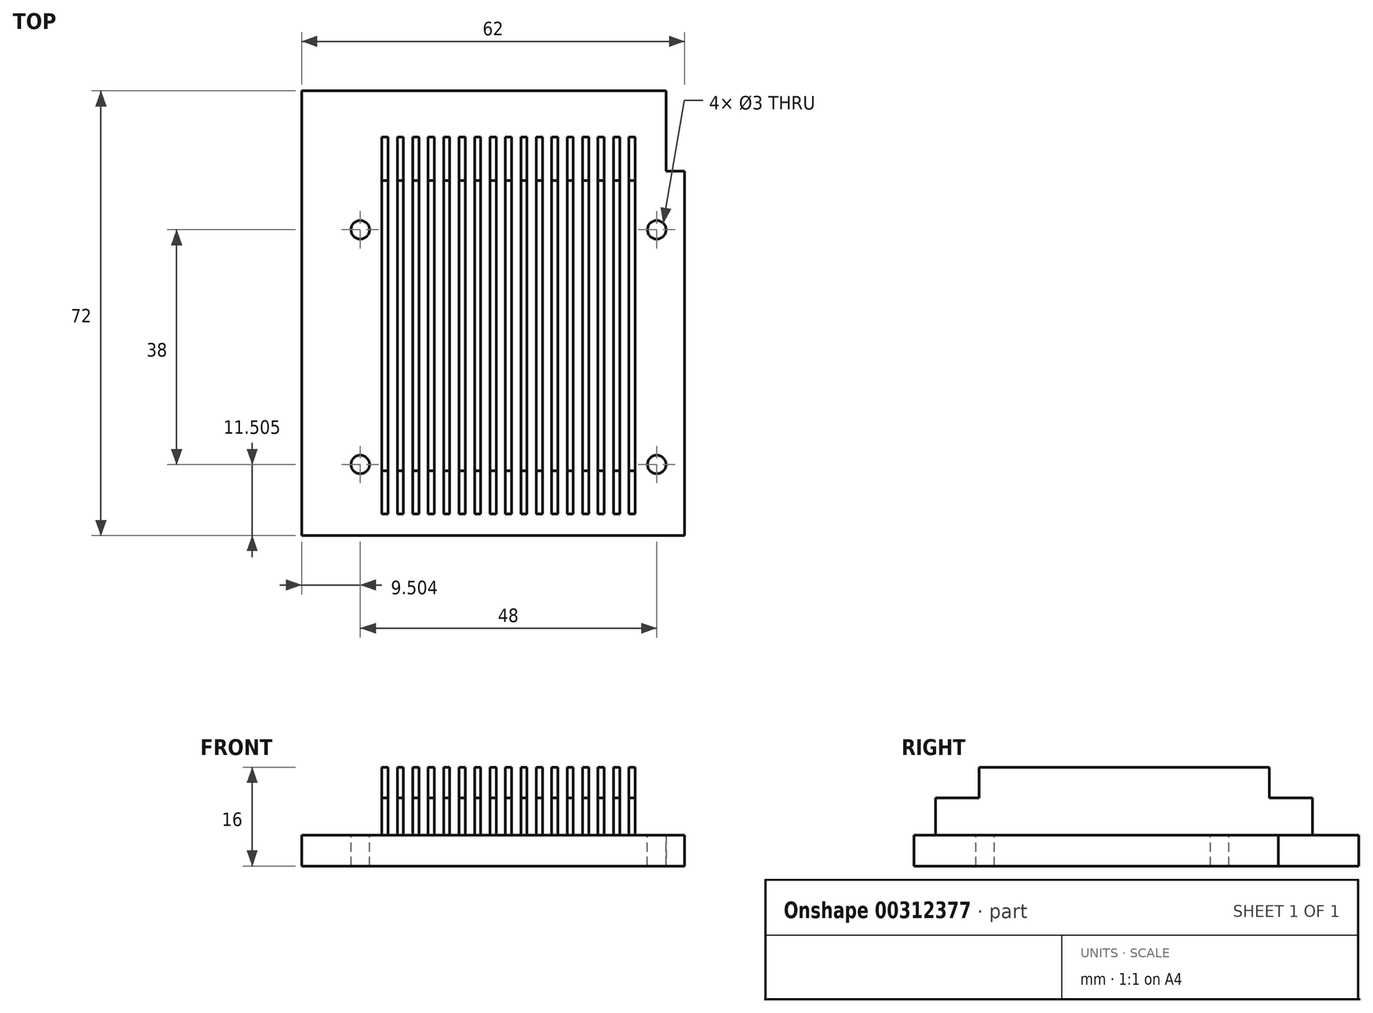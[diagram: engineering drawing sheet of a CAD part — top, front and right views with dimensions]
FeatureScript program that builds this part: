
annotation { "Feature Type Name" : "Feature", "Feature Type Description" : "" }
export const myFeature = defineFeature(function(context is Context, id is Id, definition is map)
    precondition{}
    {
        {
            var Q0;
            Q0=qCreatedBy(makeId("Top.planeOp"),FACE);
            var sketch = newSketch(context, id + "F0", { "sketchPlane" : qUnion([Q0])});
            skLineSegment(sketch, "E0", {"start": v(-50.22, 49.8) * mm, "end": v(-50.22, -22.2) * mm});
            skLineSegment(sketch, "E1", {"start": v(-50.22, 49.8) * mm, "end": v(8.78, 49.8) * mm});
            skLineSegment(sketch, "E2", {"start": v(8.78, 49.8) * mm, "end": v(8.78, 36.8) * mm});
            skLineSegment(sketch, "E3", {"start": v(8.78, 36.8) * mm, "end": v(11.78, 36.8) * mm});
            skLineSegment(sketch, "E4", {"start": v(11.78, 36.8) * mm, "end": v(11.78, -22.2) * mm});
            skLineSegment(sketch, "E5", {"start": v(-50.22, -22.2) * mm, "end": v(11.78, -22.2) * mm});
            skSolve(sketch);
        }
        {
            var Q0;
            Q0=makeQuery(id+"F0.imprint","IMPRINT",FACE,{"disambiguationData":[TD([[makeQuery(id+"F0.imprint","IMPRINT",EDGE,{"derivedFrom":sQuery(id+"F0.wireOp",EDGE,"E0")}),1.0]])]});
            extrude(context, id + "F1", {"entities" : qUnion([Q0]), "depth" : 5 * mm});
        }
        {
            var Q0;
            Q0=makeQuery(id+"F1.opExtrude","CAP_FACE",FACE,{"disambiguationData":[OSD([sQuery(id+"F0.wireOp",EDGE,"E0"),sQuery(id+"F0.wireOp",EDGE,"E1"),sQuery(id+"F0.wireOp",EDGE,"E2"),sQuery(id+"F0.wireOp",EDGE,"E3"),sQuery(id+"F0.wireOp",EDGE,"E4"),sQuery(id+"F0.wireOp",EDGE,"E5")])],"isStart":false});
            var sketch = newSketch(context, id + "F2", { "sketchPlane" : qUnion([Q0])});
            skLineSegment(sketch, "E6", {"start": v(-50.22, 13.8) * mm, "end": v(-37.22, 13.8) * mm});
            skPoint(sketch, "E6.endSnap0", {"position": v(-50.22, 13.8) * mm});
            skLineSegment(sketch, "E7", {"start": v(-20.72, 49.8) * mm, "end": v(-20.72, 42.3) * mm});
            skLineSegment(sketch, "E8", {"start": v(-19.22, -22.2) * mm, "end": v(-19.22, -18.7) * mm});
            skLineSegment(sketch, "E9", {"start": v(-37.22, 13.8) * mm, "end": v(-37.22, 42.3) * mm});
            skLineSegment(sketch, "E10", {"start": v(-37.22, 42.3) * mm, "end": v(-36.22, 42.3) * mm});
            skLineSegment(sketch, "E11", {"start": v(-36.22, 42.3) * mm, "end": v(-36.22, -18.7) * mm});
            skLineSegment(sketch, "E12", {"start": v(-36.22, -18.7) * mm, "end": v(-37.22, -18.7) * mm});
            skLineSegment(sketch, "E13", {"start": v(-37.22, -18.7) * mm, "end": v(-37.22, 13.8) * mm});
            skLineSegment(sketch, "E14", {"start": v(-36.22, 35.3) * mm, "end": v(-37.22, 35.3) * mm});
            skLineSegment(sketch, "E15", {"start": v(-36.22, -11.7) * mm, "end": v(-37.22, -11.7) * mm});
            skLineSegment(sketch, "E16.1.0.0", {"start": v(-33.72, 42.3) * mm, "end": v(-33.72, -18.7) * mm});
            skLineSegment(sketch, "E16.1.0.1", {"start": v(-34.72, 13.8) * mm, "end": v(-34.72, 42.3) * mm});
            skLineSegment(sketch, "E16.1.0.2", {"start": v(-34.72, -18.7) * mm, "end": v(-34.72, 13.8) * mm});
            skLineSegment(sketch, "E16.1.0.3", {"start": v(-33.72, 35.3) * mm, "end": v(-34.72, 35.3) * mm});
            skLineSegment(sketch, "E16.1.0.4", {"start": v(-33.72, -11.7) * mm, "end": v(-34.72, -11.7) * mm});
            skLineSegment(sketch, "E16.1.0.5", {"start": v(-33.72, -18.7) * mm, "end": v(-34.72, -18.7) * mm});
            skLineSegment(sketch, "E16.1.0.6", {"start": v(-34.72, 42.3) * mm, "end": v(-33.72, 42.3) * mm});
            skLineSegment(sketch, "E16.2.0.0", {"start": v(-31.22, 42.3) * mm, "end": v(-31.22, -18.7) * mm});
            skLineSegment(sketch, "E16.2.0.1", {"start": v(-32.22, 13.8) * mm, "end": v(-32.22, 42.3) * mm});
            skLineSegment(sketch, "E16.2.0.2", {"start": v(-32.22, -18.7) * mm, "end": v(-32.22, 13.8) * mm});
            skLineSegment(sketch, "E16.2.0.3", {"start": v(-31.22, 35.3) * mm, "end": v(-32.22, 35.3) * mm});
            skLineSegment(sketch, "E16.2.0.4", {"start": v(-31.22, -11.7) * mm, "end": v(-32.22, -11.7) * mm});
            skLineSegment(sketch, "E16.2.0.5", {"start": v(-31.22, -18.7) * mm, "end": v(-32.22, -18.7) * mm});
            skLineSegment(sketch, "E16.2.0.6", {"start": v(-32.22, 42.3) * mm, "end": v(-31.22, 42.3) * mm});
            skLineSegment(sketch, "E16.3.0.0", {"start": v(-28.72, 42.3) * mm, "end": v(-28.72, -18.7) * mm});
            skLineSegment(sketch, "E16.3.0.1", {"start": v(-29.72, 13.8) * mm, "end": v(-29.72, 42.3) * mm});
            skLineSegment(sketch, "E16.3.0.2", {"start": v(-29.72, -18.7) * mm, "end": v(-29.72, 13.8) * mm});
            skLineSegment(sketch, "E16.3.0.3", {"start": v(-28.72, 35.3) * mm, "end": v(-29.72, 35.3) * mm});
            skLineSegment(sketch, "E16.3.0.4", {"start": v(-28.72, -11.7) * mm, "end": v(-29.72, -11.7) * mm});
            skLineSegment(sketch, "E16.3.0.5", {"start": v(-28.72, -18.7) * mm, "end": v(-29.72, -18.7) * mm});
            skLineSegment(sketch, "E16.3.0.6", {"start": v(-29.72, 42.3) * mm, "end": v(-28.72, 42.3) * mm});
            skLineSegment(sketch, "E16.4.0.0", {"start": v(-26.22, 42.3) * mm, "end": v(-26.22, -18.7) * mm});
            skLineSegment(sketch, "E16.4.0.1", {"start": v(-27.22, 13.8) * mm, "end": v(-27.22, 42.3) * mm});
            skLineSegment(sketch, "E16.4.0.2", {"start": v(-27.22, -18.7) * mm, "end": v(-27.22, 13.8) * mm});
            skLineSegment(sketch, "E16.4.0.3", {"start": v(-26.22, 35.3) * mm, "end": v(-27.22, 35.3) * mm});
            skLineSegment(sketch, "E16.4.0.4", {"start": v(-26.22, -11.7) * mm, "end": v(-27.22, -11.7) * mm});
            skLineSegment(sketch, "E16.4.0.5", {"start": v(-26.22, -18.7) * mm, "end": v(-27.22, -18.7) * mm});
            skLineSegment(sketch, "E16.4.0.6", {"start": v(-27.22, 42.3) * mm, "end": v(-26.22, 42.3) * mm});
            skLineSegment(sketch, "E16.5.0.0", {"start": v(-23.72, 42.3) * mm, "end": v(-23.72, -18.7) * mm});
            skLineSegment(sketch, "E16.5.0.1", {"start": v(-24.72, 13.8) * mm, "end": v(-24.72, 42.3) * mm});
            skLineSegment(sketch, "E16.5.0.2", {"start": v(-24.72, -18.7) * mm, "end": v(-24.72, 13.8) * mm});
            skLineSegment(sketch, "E16.5.0.3", {"start": v(-23.72, 35.3) * mm, "end": v(-24.72, 35.3) * mm});
            skLineSegment(sketch, "E16.5.0.4", {"start": v(-23.72, -11.7) * mm, "end": v(-24.72, -11.7) * mm});
            skLineSegment(sketch, "E16.5.0.5", {"start": v(-23.72, -18.7) * mm, "end": v(-24.72, -18.7) * mm});
            skLineSegment(sketch, "E16.5.0.6", {"start": v(-24.72, 42.3) * mm, "end": v(-23.72, 42.3) * mm});
            skLineSegment(sketch, "E16.6.0.0", {"start": v(-21.22, 42.3) * mm, "end": v(-21.22, -18.7) * mm});
            skLineSegment(sketch, "E16.6.0.1", {"start": v(-22.22, 13.8) * mm, "end": v(-22.22, 42.3) * mm});
            skLineSegment(sketch, "E16.6.0.2", {"start": v(-22.22, -18.7) * mm, "end": v(-22.22, 13.8) * mm});
            skLineSegment(sketch, "E16.6.0.3", {"start": v(-21.22, 35.3) * mm, "end": v(-22.22, 35.3) * mm});
            skLineSegment(sketch, "E16.6.0.4", {"start": v(-21.22, -11.7) * mm, "end": v(-22.22, -11.7) * mm});
            skLineSegment(sketch, "E16.6.0.5", {"start": v(-21.22, -18.7) * mm, "end": v(-22.22, -18.7) * mm});
            skLineSegment(sketch, "E16.6.0.6", {"start": v(-22.22, 42.3) * mm, "end": v(-21.22, 42.3) * mm});
            skLineSegment(sketch, "E16.7.0.0", {"start": v(-18.72, 42.3) * mm, "end": v(-18.72, -18.7) * mm});
            skLineSegment(sketch, "E16.7.0.1", {"start": v(-19.72, 13.8) * mm, "end": v(-19.72, 42.3) * mm});
            skLineSegment(sketch, "E16.7.0.2", {"start": v(-19.72, -18.7) * mm, "end": v(-19.72, 13.8) * mm});
            skLineSegment(sketch, "E16.7.0.3", {"start": v(-18.72, 35.3) * mm, "end": v(-19.72, 35.3) * mm});
            skLineSegment(sketch, "E16.7.0.4", {"start": v(-18.72, -11.7) * mm, "end": v(-19.72, -11.7) * mm});
            skLineSegment(sketch, "E16.7.0.5", {"start": v(-18.72, -18.7) * mm, "end": v(-19.72, -18.7) * mm});
            skLineSegment(sketch, "E16.7.0.6", {"start": v(-19.72, 42.3) * mm, "end": v(-18.72, 42.3) * mm});
            skLineSegment(sketch, "E16.8.0.0", {"start": v(-16.22, 42.3) * mm, "end": v(-16.22, -18.7) * mm});
            skLineSegment(sketch, "E16.8.0.1", {"start": v(-17.22, 13.8) * mm, "end": v(-17.22, 42.3) * mm});
            skLineSegment(sketch, "E16.8.0.2", {"start": v(-17.22, -18.7) * mm, "end": v(-17.22, 13.8) * mm});
            skLineSegment(sketch, "E16.8.0.3", {"start": v(-16.22, 35.3) * mm, "end": v(-17.22, 35.3) * mm});
            skLineSegment(sketch, "E16.8.0.4", {"start": v(-16.22, -11.7) * mm, "end": v(-17.22, -11.7) * mm});
            skLineSegment(sketch, "E16.8.0.5", {"start": v(-16.22, -18.7) * mm, "end": v(-17.22, -18.7) * mm});
            skLineSegment(sketch, "E16.8.0.6", {"start": v(-17.22, 42.3) * mm, "end": v(-16.22, 42.3) * mm});
            skLineSegment(sketch, "E16.9.0.0", {"start": v(-13.72, 42.3) * mm, "end": v(-13.72, -18.7) * mm});
            skLineSegment(sketch, "E16.9.0.1", {"start": v(-14.72, 13.8) * mm, "end": v(-14.72, 42.3) * mm});
            skLineSegment(sketch, "E16.9.0.2", {"start": v(-14.72, -18.7) * mm, "end": v(-14.72, 13.8) * mm});
            skLineSegment(sketch, "E16.9.0.3", {"start": v(-13.72, 35.3) * mm, "end": v(-14.72, 35.3) * mm});
            skLineSegment(sketch, "E16.9.0.4", {"start": v(-13.72, -11.7) * mm, "end": v(-14.72, -11.7) * mm});
            skLineSegment(sketch, "E16.9.0.5", {"start": v(-13.72, -18.7) * mm, "end": v(-14.72, -18.7) * mm});
            skLineSegment(sketch, "E16.9.0.6", {"start": v(-14.72, 42.3) * mm, "end": v(-13.72, 42.3) * mm});
            skLineSegment(sketch, "E16.10.0.0", {"start": v(-11.22, 42.3) * mm, "end": v(-11.22, -18.7) * mm});
            skLineSegment(sketch, "E16.10.0.1", {"start": v(-12.22, 13.8) * mm, "end": v(-12.22, 42.3) * mm});
            skLineSegment(sketch, "E16.10.0.2", {"start": v(-12.22, -18.7) * mm, "end": v(-12.22, 13.8) * mm});
            skLineSegment(sketch, "E16.10.0.3", {"start": v(-11.22, 35.3) * mm, "end": v(-12.22, 35.3) * mm});
            skLineSegment(sketch, "E16.10.0.4", {"start": v(-11.22, -11.7) * mm, "end": v(-12.22, -11.7) * mm});
            skLineSegment(sketch, "E16.10.0.5", {"start": v(-11.22, -18.7) * mm, "end": v(-12.22, -18.7) * mm});
            skLineSegment(sketch, "E16.10.0.6", {"start": v(-12.22, 42.3) * mm, "end": v(-11.22, 42.3) * mm});
            skLineSegment(sketch, "E16.11.0.0", {"start": v(-8.72, 42.3) * mm, "end": v(-8.72, -18.7) * mm});
            skLineSegment(sketch, "E16.11.0.1", {"start": v(-9.72, 13.8) * mm, "end": v(-9.72, 42.3) * mm});
            skLineSegment(sketch, "E16.11.0.2", {"start": v(-9.72, -18.7) * mm, "end": v(-9.72, 13.8) * mm});
            skLineSegment(sketch, "E16.11.0.3", {"start": v(-8.72, 35.3) * mm, "end": v(-9.72, 35.3) * mm});
            skLineSegment(sketch, "E16.11.0.4", {"start": v(-8.72, -11.7) * mm, "end": v(-9.72, -11.7) * mm});
            skLineSegment(sketch, "E16.11.0.5", {"start": v(-8.72, -18.7) * mm, "end": v(-9.72, -18.7) * mm});
            skLineSegment(sketch, "E16.11.0.6", {"start": v(-9.72, 42.3) * mm, "end": v(-8.72, 42.3) * mm});
            skLineSegment(sketch, "E16.12.0.0", {"start": v(-6.22, 42.3) * mm, "end": v(-6.22, -18.7) * mm});
            skLineSegment(sketch, "E16.12.0.1", {"start": v(-7.22, 13.8) * mm, "end": v(-7.22, 42.3) * mm});
            skLineSegment(sketch, "E16.12.0.2", {"start": v(-7.22, -18.7) * mm, "end": v(-7.22, 13.8) * mm});
            skLineSegment(sketch, "E16.12.0.3", {"start": v(-6.22, 35.3) * mm, "end": v(-7.22, 35.3) * mm});
            skLineSegment(sketch, "E16.12.0.4", {"start": v(-6.22, -11.7) * mm, "end": v(-7.22, -11.7) * mm});
            skLineSegment(sketch, "E16.12.0.5", {"start": v(-6.22, -18.7) * mm, "end": v(-7.22, -18.7) * mm});
            skLineSegment(sketch, "E16.12.0.6", {"start": v(-7.22, 42.3) * mm, "end": v(-6.22, 42.3) * mm});
            skLineSegment(sketch, "E16.13.0.0", {"start": v(-3.72, 42.3) * mm, "end": v(-3.72, -18.7) * mm});
            skLineSegment(sketch, "E16.13.0.1", {"start": v(-4.72, 13.8) * mm, "end": v(-4.72, 42.3) * mm});
            skLineSegment(sketch, "E16.13.0.2", {"start": v(-4.72, -18.7) * mm, "end": v(-4.72, 13.8) * mm});
            skLineSegment(sketch, "E16.13.0.3", {"start": v(-3.72, 35.3) * mm, "end": v(-4.72, 35.3) * mm});
            skLineSegment(sketch, "E16.13.0.4", {"start": v(-3.72, -11.7) * mm, "end": v(-4.72, -11.7) * mm});
            skLineSegment(sketch, "E16.13.0.5", {"start": v(-3.72, -18.7) * mm, "end": v(-4.72, -18.7) * mm});
            skLineSegment(sketch, "E16.13.0.6", {"start": v(-4.72, 42.3) * mm, "end": v(-3.72, 42.3) * mm});
            skLineSegment(sketch, "E16.14.0.0", {"start": v(-1.22, 42.3) * mm, "end": v(-1.22, -18.7) * mm});
            skLineSegment(sketch, "E16.14.0.1", {"start": v(-2.22, 13.8) * mm, "end": v(-2.22, 42.3) * mm});
            skLineSegment(sketch, "E16.14.0.2", {"start": v(-2.22, -18.7) * mm, "end": v(-2.22, 13.8) * mm});
            skLineSegment(sketch, "E16.14.0.3", {"start": v(-1.22, 35.3) * mm, "end": v(-2.22, 35.3) * mm});
            skLineSegment(sketch, "E16.14.0.4", {"start": v(-1.22, -11.7) * mm, "end": v(-2.22, -11.7) * mm});
            skLineSegment(sketch, "E16.14.0.5", {"start": v(-1.22, -18.7) * mm, "end": v(-2.22, -18.7) * mm});
            skLineSegment(sketch, "E16.14.0.6", {"start": v(-2.22, 42.3) * mm, "end": v(-1.22, 42.3) * mm});
            skLineSegment(sketch, "E16.15.0.0", {"start": v(1.28, 42.3) * mm, "end": v(1.28, -18.7) * mm});
            skLineSegment(sketch, "E16.15.0.1", {"start": v(0.28, 13.8) * mm, "end": v(0.28, 42.3) * mm});
            skLineSegment(sketch, "E16.15.0.2", {"start": v(0.28, -18.7) * mm, "end": v(0.28, 13.8) * mm});
            skLineSegment(sketch, "E16.15.0.3", {"start": v(1.28, 35.3) * mm, "end": v(0.28, 35.3) * mm});
            skLineSegment(sketch, "E16.15.0.4", {"start": v(1.28, -11.7) * mm, "end": v(0.28, -11.7) * mm});
            skLineSegment(sketch, "E16.15.0.5", {"start": v(1.28, -18.7) * mm, "end": v(0.28, -18.7) * mm});
            skLineSegment(sketch, "E16.15.0.6", {"start": v(0.28, 42.3) * mm, "end": v(1.28, 42.3) * mm});
            skLineSegment(sketch, "E16.16.0.0", {"start": v(3.78, 42.3) * mm, "end": v(3.78, -18.7) * mm});
            skLineSegment(sketch, "E16.16.0.1", {"start": v(2.78, 13.8) * mm, "end": v(2.78, 42.3) * mm});
            skLineSegment(sketch, "E16.16.0.2", {"start": v(2.78, -18.7) * mm, "end": v(2.78, 13.8) * mm});
            skLineSegment(sketch, "E16.16.0.3", {"start": v(3.78, 35.3) * mm, "end": v(2.78, 35.3) * mm});
            skLineSegment(sketch, "E16.16.0.4", {"start": v(3.78, -11.7) * mm, "end": v(2.78, -11.7) * mm});
            skLineSegment(sketch, "E16.16.0.5", {"start": v(3.78, -18.7) * mm, "end": v(2.78, -18.7) * mm});
            skLineSegment(sketch, "E16.16.0.6", {"start": v(2.78, 42.3) * mm, "end": v(3.78, 42.3) * mm});
            skLineSegment(sketch, "E16.direction1", {"start": v(-37.22, -18.7) * mm, "end": v(-34.72, -18.7) * mm, "construction": true});
            skLineSegment(sketch, "E17", {"start": v(-50.22, -22.2) * mm, "end": v(-40.72, -22.2) * mm});
            skLineSegment(sketch, "E18", {"start": v(-40.72, -22.2) * mm, "end": v(-40.72, -10.7) * mm});
            skLineSegment(sketch, "E19", {"start": v(-40.72, -10.7) * mm, "end": v(-40.72, 27.3) * mm});
            skLineSegment(sketch, "E20", {"start": v(11.78, -22.2) * mm, "end": v(7.28, -22.2) * mm});
            skLineSegment(sketch, "E21", {"start": v(7.28, -22.2) * mm, "end": v(7.28, -10.7) * mm});
            skLineSegment(sketch, "E22", {"start": v(7.28, -10.7) * mm, "end": v(7.28, 27.3) * mm});
            skSolve(sketch);
        }
        {
            var Q0;
            {var subQ4=sQuery(id+"F2.wireOp",EDGE,"E14");Q0=makeQuery(id+"F2.imprint","IMPRINT",FACE,{"disambiguationData":[TD([[makeQuery(id+"F2.imprint","IMPRINT",EDGE,{"derivedFrom":subQ4}),1.0]])]});}
            var Q1;
            {var subQ0=sQuery(id+"F2.wireOp",EDGE,"E16.1.0.3");Q1=makeQuery(id+"F2.imprint","IMPRINT",FACE,{"disambiguationData":[TD([[makeQuery(id+"F2.imprint","IMPRINT",EDGE,{"derivedFrom":subQ0}),1.0]])]});}
            var Q2;
            {var subQ0=sQuery(id+"F2.wireOp",EDGE,"E16.2.0.3");Q2=makeQuery(id+"F2.imprint","IMPRINT",FACE,{"disambiguationData":[TD([[makeQuery(id+"F2.imprint","IMPRINT",EDGE,{"derivedFrom":subQ0}),1.0]])]});}
            var Q3;
            {var subQ0=sQuery(id+"F2.wireOp",EDGE,"E16.3.0.3");Q3=makeQuery(id+"F2.imprint","IMPRINT",FACE,{"disambiguationData":[TD([[makeQuery(id+"F2.imprint","IMPRINT",EDGE,{"derivedFrom":subQ0}),1.0]])]});}
            var Q4;
            {var subQ0=sQuery(id+"F2.wireOp",EDGE,"E16.4.0.3");Q4=makeQuery(id+"F2.imprint","IMPRINT",FACE,{"disambiguationData":[TD([[makeQuery(id+"F2.imprint","IMPRINT",EDGE,{"derivedFrom":subQ0}),1.0]])]});}
            var Q5;
            {var subQ0=sQuery(id+"F2.wireOp",EDGE,"E16.5.0.3");Q5=makeQuery(id+"F2.imprint","IMPRINT",FACE,{"disambiguationData":[TD([[makeQuery(id+"F2.imprint","IMPRINT",EDGE,{"derivedFrom":subQ0}),1.0]])]});}
            var Q6;
            {var subQ0=sQuery(id+"F2.wireOp",EDGE,"E16.6.0.3");Q6=makeQuery(id+"F2.imprint","IMPRINT",FACE,{"disambiguationData":[TD([[makeQuery(id+"F2.imprint","IMPRINT",EDGE,{"derivedFrom":subQ0}),1.0]])]});}
            var Q7;
            {var subQ0=sQuery(id+"F2.wireOp",EDGE,"E16.7.0.3");Q7=makeQuery(id+"F2.imprint","IMPRINT",FACE,{"disambiguationData":[TD([[makeQuery(id+"F2.imprint","IMPRINT",EDGE,{"derivedFrom":subQ0}),1.0]])]});}
            var Q8;
            {var subQ0=sQuery(id+"F2.wireOp",EDGE,"E16.8.0.3");Q8=makeQuery(id+"F2.imprint","IMPRINT",FACE,{"disambiguationData":[TD([[makeQuery(id+"F2.imprint","IMPRINT",EDGE,{"derivedFrom":subQ0}),1.0]])]});}
            var Q9;
            {var subQ0=sQuery(id+"F2.wireOp",EDGE,"E16.9.0.3");Q9=makeQuery(id+"F2.imprint","IMPRINT",FACE,{"disambiguationData":[TD([[makeQuery(id+"F2.imprint","IMPRINT",EDGE,{"derivedFrom":subQ0}),1.0]])]});}
            var Q10;
            {var subQ0=sQuery(id+"F2.wireOp",EDGE,"E16.10.0.3");Q10=makeQuery(id+"F2.imprint","IMPRINT",FACE,{"disambiguationData":[TD([[makeQuery(id+"F2.imprint","IMPRINT",EDGE,{"derivedFrom":subQ0}),1.0]])]});}
            var Q11;
            {var subQ0=sQuery(id+"F2.wireOp",EDGE,"E16.11.0.3");Q11=makeQuery(id+"F2.imprint","IMPRINT",FACE,{"disambiguationData":[TD([[makeQuery(id+"F2.imprint","IMPRINT",EDGE,{"derivedFrom":subQ0}),1.0]])]});}
            var Q12;
            {var subQ0=sQuery(id+"F2.wireOp",EDGE,"E16.12.0.3");Q12=makeQuery(id+"F2.imprint","IMPRINT",FACE,{"disambiguationData":[TD([[makeQuery(id+"F2.imprint","IMPRINT",EDGE,{"derivedFrom":subQ0}),1.0]])]});}
            var Q13;
            {var subQ0=sQuery(id+"F2.wireOp",EDGE,"E16.13.0.3");Q13=makeQuery(id+"F2.imprint","IMPRINT",FACE,{"disambiguationData":[TD([[makeQuery(id+"F2.imprint","IMPRINT",EDGE,{"derivedFrom":subQ0}),1.0]])]});}
            var Q14;
            {var subQ0=sQuery(id+"F2.wireOp",EDGE,"E16.14.0.3");Q14=makeQuery(id+"F2.imprint","IMPRINT",FACE,{"disambiguationData":[TD([[makeQuery(id+"F2.imprint","IMPRINT",EDGE,{"derivedFrom":subQ0}),1.0]])]});}
            var Q15;
            {var subQ0=sQuery(id+"F2.wireOp",EDGE,"E16.15.0.3");Q15=makeQuery(id+"F2.imprint","IMPRINT",FACE,{"disambiguationData":[TD([[makeQuery(id+"F2.imprint","IMPRINT",EDGE,{"derivedFrom":subQ0}),1.0]])]});}
            var Q16;
            {var subQ0=sQuery(id+"F2.wireOp",EDGE,"E16.16.0.3");Q16=makeQuery(id+"F2.imprint","IMPRINT",FACE,{"disambiguationData":[TD([[makeQuery(id+"F2.imprint","IMPRINT",EDGE,{"derivedFrom":subQ0}),1.0]])]});}
            extrude(context, id + "F3", {"entities" : qUnion([Q0, Q1, Q2, Q3, Q4, Q5, Q6, Q7, Q8, Q9, Q10, Q11, Q12, Q13, Q14, Q15, Q16]), "operationType" : NewBodyOperationType.ADD, "depth" : 11 * mm});
        }
        {
            var Q0;
            {var subQ0=sQuery(id+"F2.wireOp",EDGE,"E10");Q0=makeQuery(id+"F2.imprint","IMPRINT",FACE,{"disambiguationData":[TD([[makeQuery(id+"F2.imprint","IMPRINT",EDGE,{"derivedFrom":subQ0}),-1.0]])]});}
            var Q1;
            {var subQ2=sQuery(id+"F2.wireOp",EDGE,"E16.1.0.3");Q1=makeQuery(id+"F2.imprint","IMPRINT",FACE,{"disambiguationData":[TD([[makeQuery(id+"F2.imprint","IMPRINT",EDGE,{"derivedFrom":subQ2}),-1.0]])]});}
            var Q2;
            {var subQ2=sQuery(id+"F2.wireOp",EDGE,"E16.2.0.3");Q2=makeQuery(id+"F2.imprint","IMPRINT",FACE,{"disambiguationData":[TD([[makeQuery(id+"F2.imprint","IMPRINT",EDGE,{"derivedFrom":subQ2}),-1.0]])]});}
            var Q3;
            {var subQ2=sQuery(id+"F2.wireOp",EDGE,"E16.3.0.3");Q3=makeQuery(id+"F2.imprint","IMPRINT",FACE,{"disambiguationData":[TD([[makeQuery(id+"F2.imprint","IMPRINT",EDGE,{"derivedFrom":subQ2}),-1.0]])]});}
            var Q4;
            {var subQ2=sQuery(id+"F2.wireOp",EDGE,"E16.4.0.3");Q4=makeQuery(id+"F2.imprint","IMPRINT",FACE,{"disambiguationData":[TD([[makeQuery(id+"F2.imprint","IMPRINT",EDGE,{"derivedFrom":subQ2}),-1.0]])]});}
            var Q5;
            {var subQ2=sQuery(id+"F2.wireOp",EDGE,"E16.5.0.3");Q5=makeQuery(id+"F2.imprint","IMPRINT",FACE,{"disambiguationData":[TD([[makeQuery(id+"F2.imprint","IMPRINT",EDGE,{"derivedFrom":subQ2}),-1.0]])]});}
            var Q6;
            {var subQ2=sQuery(id+"F2.wireOp",EDGE,"E16.6.0.3");Q6=makeQuery(id+"F2.imprint","IMPRINT",FACE,{"disambiguationData":[TD([[makeQuery(id+"F2.imprint","IMPRINT",EDGE,{"derivedFrom":subQ2}),-1.0]])]});}
            var Q7;
            {var subQ2=sQuery(id+"F2.wireOp",EDGE,"E16.7.0.3");Q7=makeQuery(id+"F2.imprint","IMPRINT",FACE,{"disambiguationData":[TD([[makeQuery(id+"F2.imprint","IMPRINT",EDGE,{"derivedFrom":subQ2}),-1.0]])]});}
            var Q8;
            {var subQ2=sQuery(id+"F2.wireOp",EDGE,"E16.8.0.3");Q8=makeQuery(id+"F2.imprint","IMPRINT",FACE,{"disambiguationData":[TD([[makeQuery(id+"F2.imprint","IMPRINT",EDGE,{"derivedFrom":subQ2}),-1.0]])]});}
            var Q9;
            {var subQ2=sQuery(id+"F2.wireOp",EDGE,"E16.9.0.3");Q9=makeQuery(id+"F2.imprint","IMPRINT",FACE,{"disambiguationData":[TD([[makeQuery(id+"F2.imprint","IMPRINT",EDGE,{"derivedFrom":subQ2}),-1.0]])]});}
            var Q10;
            {var subQ2=sQuery(id+"F2.wireOp",EDGE,"E16.10.0.3");Q10=makeQuery(id+"F2.imprint","IMPRINT",FACE,{"disambiguationData":[TD([[makeQuery(id+"F2.imprint","IMPRINT",EDGE,{"derivedFrom":subQ2}),-1.0]])]});}
            var Q11;
            {var subQ2=sQuery(id+"F2.wireOp",EDGE,"E16.11.0.3");Q11=makeQuery(id+"F2.imprint","IMPRINT",FACE,{"disambiguationData":[TD([[makeQuery(id+"F2.imprint","IMPRINT",EDGE,{"derivedFrom":subQ2}),-1.0]])]});}
            var Q12;
            {var subQ2=sQuery(id+"F2.wireOp",EDGE,"E16.12.0.3");Q12=makeQuery(id+"F2.imprint","IMPRINT",FACE,{"disambiguationData":[TD([[makeQuery(id+"F2.imprint","IMPRINT",EDGE,{"derivedFrom":subQ2}),-1.0]])]});}
            var Q13;
            {var subQ2=sQuery(id+"F2.wireOp",EDGE,"E16.13.0.3");Q13=makeQuery(id+"F2.imprint","IMPRINT",FACE,{"disambiguationData":[TD([[makeQuery(id+"F2.imprint","IMPRINT",EDGE,{"derivedFrom":subQ2}),-1.0]])]});}
            var Q14;
            {var subQ2=sQuery(id+"F2.wireOp",EDGE,"E16.14.0.3");Q14=makeQuery(id+"F2.imprint","IMPRINT",FACE,{"disambiguationData":[TD([[makeQuery(id+"F2.imprint","IMPRINT",EDGE,{"derivedFrom":subQ2}),-1.0]])]});}
            var Q15;
            {var subQ2=sQuery(id+"F2.wireOp",EDGE,"E16.15.0.3");Q15=makeQuery(id+"F2.imprint","IMPRINT",FACE,{"disambiguationData":[TD([[makeQuery(id+"F2.imprint","IMPRINT",EDGE,{"derivedFrom":subQ2}),-1.0]])]});}
            var Q16;
            {var subQ2=sQuery(id+"F2.wireOp",EDGE,"E16.16.0.3");Q16=makeQuery(id+"F2.imprint","IMPRINT",FACE,{"disambiguationData":[TD([[makeQuery(id+"F2.imprint","IMPRINT",EDGE,{"derivedFrom":subQ2}),-1.0]])]});}
            var Q17;
            {var subQ2=sQuery(id+"F2.wireOp",EDGE,"E16.16.0.4");Q17=makeQuery(id+"F2.imprint","IMPRINT",FACE,{"disambiguationData":[TD([[makeQuery(id+"F2.imprint","IMPRINT",EDGE,{"derivedFrom":subQ2}),1.0]])]});}
            var Q18;
            {var subQ2=sQuery(id+"F2.wireOp",EDGE,"E16.15.0.4");Q18=makeQuery(id+"F2.imprint","IMPRINT",FACE,{"disambiguationData":[TD([[makeQuery(id+"F2.imprint","IMPRINT",EDGE,{"derivedFrom":subQ2}),1.0]])]});}
            var Q19;
            {var subQ2=sQuery(id+"F2.wireOp",EDGE,"E16.14.0.4");Q19=makeQuery(id+"F2.imprint","IMPRINT",FACE,{"disambiguationData":[TD([[makeQuery(id+"F2.imprint","IMPRINT",EDGE,{"derivedFrom":subQ2}),1.0]])]});}
            var Q20;
            {var subQ2=sQuery(id+"F2.wireOp",EDGE,"E16.13.0.4");Q20=makeQuery(id+"F2.imprint","IMPRINT",FACE,{"disambiguationData":[TD([[makeQuery(id+"F2.imprint","IMPRINT",EDGE,{"derivedFrom":subQ2}),1.0]])]});}
            var Q21;
            {var subQ2=sQuery(id+"F2.wireOp",EDGE,"E16.12.0.4");Q21=makeQuery(id+"F2.imprint","IMPRINT",FACE,{"disambiguationData":[TD([[makeQuery(id+"F2.imprint","IMPRINT",EDGE,{"derivedFrom":subQ2}),1.0]])]});}
            var Q22;
            {var subQ2=sQuery(id+"F2.wireOp",EDGE,"E16.11.0.4");Q22=makeQuery(id+"F2.imprint","IMPRINT",FACE,{"disambiguationData":[TD([[makeQuery(id+"F2.imprint","IMPRINT",EDGE,{"derivedFrom":subQ2}),1.0]])]});}
            var Q23;
            {var subQ2=sQuery(id+"F2.wireOp",EDGE,"E16.10.0.4");Q23=makeQuery(id+"F2.imprint","IMPRINT",FACE,{"disambiguationData":[TD([[makeQuery(id+"F2.imprint","IMPRINT",EDGE,{"derivedFrom":subQ2}),1.0]])]});}
            var Q24;
            {var subQ2=sQuery(id+"F2.wireOp",EDGE,"E16.9.0.4");Q24=makeQuery(id+"F2.imprint","IMPRINT",FACE,{"disambiguationData":[TD([[makeQuery(id+"F2.imprint","IMPRINT",EDGE,{"derivedFrom":subQ2}),1.0]])]});}
            var Q25;
            {var subQ2=sQuery(id+"F2.wireOp",EDGE,"E16.8.0.4");Q25=makeQuery(id+"F2.imprint","IMPRINT",FACE,{"disambiguationData":[TD([[makeQuery(id+"F2.imprint","IMPRINT",EDGE,{"derivedFrom":subQ2}),1.0]])]});}
            var Q26;
            {var subQ4=sQuery(id+"F2.wireOp",EDGE,"E16.7.0.4");Q26=makeQuery(id+"F2.imprint","IMPRINT",FACE,{"disambiguationData":[TD([[makeQuery(id+"F2.imprint","IMPRINT",EDGE,{"derivedFrom":subQ4}),1.0]])]});}
            var Q27;
            {var subQ2=sQuery(id+"F2.wireOp",EDGE,"E16.6.0.4");Q27=makeQuery(id+"F2.imprint","IMPRINT",FACE,{"disambiguationData":[TD([[makeQuery(id+"F2.imprint","IMPRINT",EDGE,{"derivedFrom":subQ2}),1.0]])]});}
            var Q28;
            {var subQ2=sQuery(id+"F2.wireOp",EDGE,"E16.5.0.4");Q28=makeQuery(id+"F2.imprint","IMPRINT",FACE,{"disambiguationData":[TD([[makeQuery(id+"F2.imprint","IMPRINT",EDGE,{"derivedFrom":subQ2}),1.0]])]});}
            var Q29;
            {var subQ2=sQuery(id+"F2.wireOp",EDGE,"E16.4.0.4");Q29=makeQuery(id+"F2.imprint","IMPRINT",FACE,{"disambiguationData":[TD([[makeQuery(id+"F2.imprint","IMPRINT",EDGE,{"derivedFrom":subQ2}),1.0]])]});}
            var Q30;
            {var subQ2=sQuery(id+"F2.wireOp",EDGE,"E16.3.0.4");Q30=makeQuery(id+"F2.imprint","IMPRINT",FACE,{"disambiguationData":[TD([[makeQuery(id+"F2.imprint","IMPRINT",EDGE,{"derivedFrom":subQ2}),1.0]])]});}
            var Q31;
            {var subQ2=sQuery(id+"F2.wireOp",EDGE,"E16.2.0.4");Q31=makeQuery(id+"F2.imprint","IMPRINT",FACE,{"disambiguationData":[TD([[makeQuery(id+"F2.imprint","IMPRINT",EDGE,{"derivedFrom":subQ2}),1.0]])]});}
            var Q32;
            {var subQ2=sQuery(id+"F2.wireOp",EDGE,"E16.1.0.4");Q32=makeQuery(id+"F2.imprint","IMPRINT",FACE,{"disambiguationData":[TD([[makeQuery(id+"F2.imprint","IMPRINT",EDGE,{"derivedFrom":subQ2}),1.0]])]});}
            var Q33;
            {var subQ0=sQuery(id+"F2.wireOp",EDGE,"E12");Q33=makeQuery(id+"F2.imprint","IMPRINT",FACE,{"disambiguationData":[TD([[makeQuery(id+"F2.imprint","IMPRINT",EDGE,{"derivedFrom":subQ0}),-1.0]])]});}
            extrude(context, id + "F4", {"entities" : qUnion([Q0, Q1, Q2, Q3, Q4, Q5, Q6, Q7, Q8, Q9, Q10, Q11, Q12, Q13, Q14, Q15, Q16, Q17, Q18, Q19, Q20, Q21, Q22, Q23, Q24, Q25, Q26, Q27, Q28, Q29, Q30, Q31, Q32, Q33]), "operationType" : NewBodyOperationType.ADD, "depth" : 6 * mm});
        }
        {
            var Q0;
            Q0=sQuery(id+"F2.wireOp",VERTEX,"E19.end");
            var Q1;
            Q1=sQuery(id+"F2.wireOp",VERTEX,"E22.end");
            var Q2;
            Q2=sQuery(id+"F2.wireOp",VERTEX,"E22.start");
            var Q3;
            Q3=sQuery(id+"F2.wireOp",VERTEX,"E19.start");
            var Q4;
            Q4=makeQuery(id+"F1.opExtrude","SWEPT_BODY",BODY,{"disambiguationData":[OSD([sQuery(id+"F0.wireOp",EDGE,"E0"),sQuery(id+"F0.wireOp",EDGE,"E1"),sQuery(id+"F0.wireOp",EDGE,"E2"),sQuery(id+"F0.wireOp",EDGE,"E3"),sQuery(id+"F0.wireOp",EDGE,"E4"),sQuery(id+"F0.wireOp",EDGE,"E5")])]});
            hole(context, id + "F5", {"style" : HoleStyle.SIMPLE, "endStyle" : HoleEndStyle.THROUGH, "holeDiameter" : 3 * mm, "tappedDepth" : 12.7 * mm, "tapClearance" : 3, "locations" : qUnion([Q0, Q1, Q2, Q3]), "scope" : qUnion([Q4])});
        }
    });
